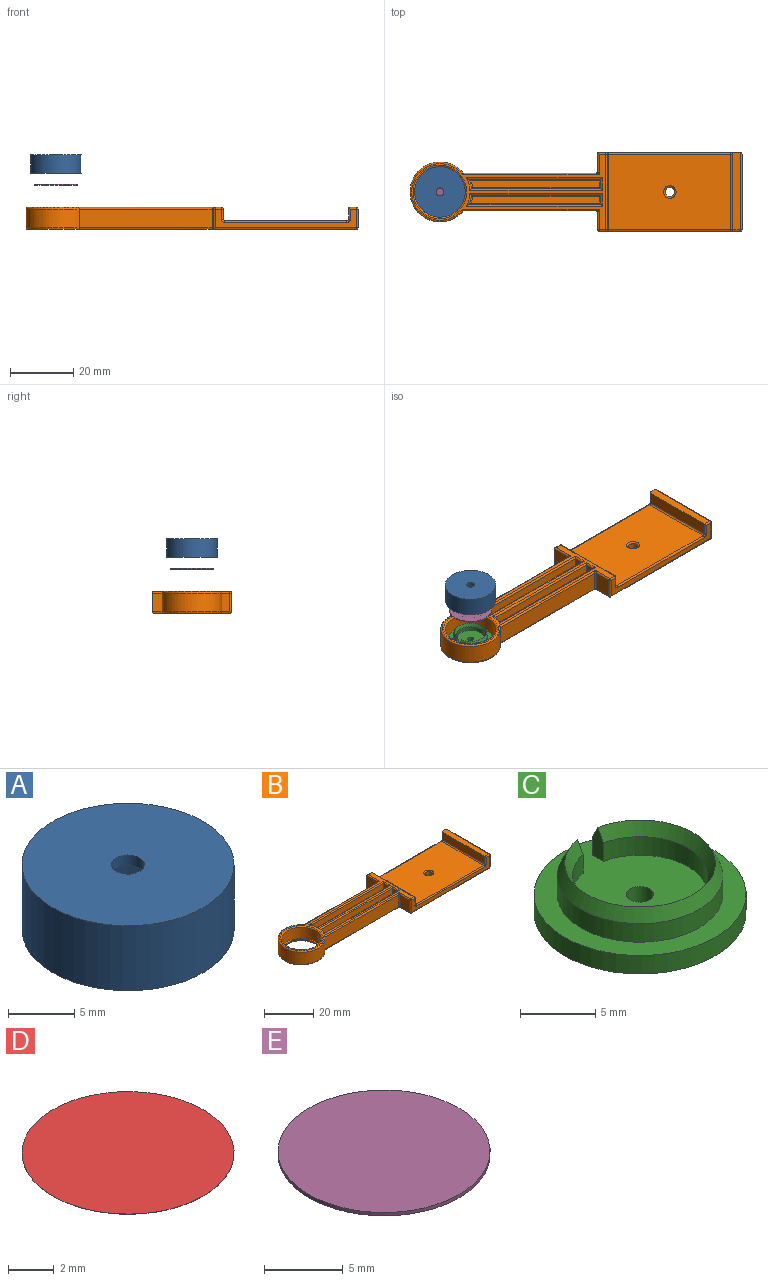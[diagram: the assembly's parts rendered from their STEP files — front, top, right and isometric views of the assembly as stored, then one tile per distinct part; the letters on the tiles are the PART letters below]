
ASSEMBLY  parts=5 mates=3
PART A: 10 faces, bbox 16x16x6 mm
  f0: plane 16x16mm, normal (0,0,-1), area 47.1mm2, adj f1,f9
  f1: cylinder r=7mm len=14mm, axis (0,0,-1), area 219.9mm2, adj f0,f2
  f2: plane 14x14mm, normal (0,0,-1), area 40.8mm2, adj f1,f3
  f3: cylinder r=6mm len=12mm, axis (0,0,-1), area 9.5mm2, adj f2,f4
  f4: cone r=5mm half-angle=54.6deg, axis (0,0,1), area 42.4mm2, adj f3,f5
  f5: cylinder r=5mm len=10mm, axis (0,0,-1), area 31.4mm2, adj f4,f6
  f6: plane 10x10mm, normal (0,0,-1), area 73.6mm2, adj f5,f7
  f7: cylinder r=1.25mm len=2.5mm, axis (0,0,-1), area 7.6mm2, adj f6,f8
  f8: plane 16x16mm, normal (0,0,1), area 196.2mm2, adj f7,f9
  f9: cylinder r=8mm len=16mm, axis (0,0,-1), area 301.6mm2, adj f0,f8
PART B: 92 faces, bbox 106.1x25x7 mm
  f0: plane 6x6mm, normal (-1,0,0), area 36mm2, adj f9,f42,f80,f81
  f1: cylinder r=8mm len=16mm, axis (0,0,1), area 276.5mm2, adj f27,f76
  f2: plane 4x3mm, normal (-1,0,0), area 12mm2, adj f20,f24,f63,f72
  f3: plane 40.6x2mm, normal (0,0,1), area 80.6mm2, adj f68,f69,f70,f71
  f4: cylinder r=10mm len=4mm, axis (0,0,1), area 12.5mm2, adj f19,f25,f64,f71
  f5: plane 61.5x24mm, normal (0,0,1), area 199.2mm2, adj f29,f30,f34,f37,f38,f42,f45,f46
  f6: plane 42.13x6mm, normal (0,-1,0), area 252.8mm2, adj f18,f30,f86,f88
  f7: plane 42.13x6mm, normal (0,1,0), area 252.8mm2, adj f18,f38,f81,f83
  f8: plane 44.8x6mm, normal (0,-1,0), area 95.8mm2, adj f28,f32,f37,f40,f44,f47,f48,f50
  f9: plane 45.3x6.5mm, normal (0,1,0), area 99.8mm2, adj f0,f15,f35,f46,f53,f55,f57,f58
  f10: cylinder r=1.5mm len=3mm, axis (0,0,-1), area 16.5mm2, adj f77,f91
  f11: plane 38.8x24mm, normal (0,0,1), area 918.6mm2, adj f51,f52,f56,f57,f77
  f12: plane 104.3x24mm, normal (0,0,-1), area 1579.5mm2, adj f31,f32,f78,f80,f82,f83,f84,f85
  f13: plane 24x3.75mm, normal (-1,0,0), area 90mm2, adj f15,f50,f56,f59
  f14: plane 24x6mm, normal (1,0,0), area 144mm2, adj f31,f35,f39,f40
  f15: plane 24.5x2.5mm, normal (0,0,1), area 61.2mm2, adj f9,f13,f39,f47,f59
  f16: plane 24x3.25mm, normal (1,0,0), area 78mm2, adj f44,f45,f52,f53
  f17: plane 6x5.5mm, normal (-1,0,0), area 33mm2, adj f28,f29,f85,f88
  f18: cylinder r=9.5mm len=19mm, axis (0,0,1), area 280.2mm2, adj f6,f7,f34,f84
  f19: plane 41.84x4mm, normal (0,1,0), area 167.3mm2, adj f4,f21,f65,f70
  f20: plane 41.84x4mm, normal (0,-1,0), area 167.3mm2, adj f2,f23,f61,f74
  f21: plane 4x3mm, normal (-1,0,0), area 12mm2, adj f19,f25,f67,f68
  f22: plane 40.6x2mm, normal (0,0,1), area 80.6mm2, adj f60,f61,f62,f63
  f23: cylinder r=10mm len=4mm, axis (0,0,1), area 12.5mm2, adj f20,f24,f60,f75
  f24: plane 41.05x4mm, normal (0,1,0), area 164.2mm2, adj f2,f23,f62,f73
  f25: plane 41.05x4mm, normal (0,-1,0), area 164.2mm2, adj f4,f21,f66,f69
  f26: cylinder r=7.5mm len=15mm, axis (0,0,-1), area 23.6mm2, adj f27,f90
  f27: plane 16x16mm, normal (0,0,1), area 24.3mm2, adj f1,f26
  f28: cylinder r=0.5mm len=6.35mm, axis (0,0,1), area 4.9mm2, adj f8,f17,f32,f33,f85
  f29: cylinder r=0.5mm len=6.5mm, axis (0,1,0), area 4.6mm2, adj f5,f17,f33,f89
  f30: cylinder r=0.5mm len=43.38mm, axis (-1,0,0), area 33.5mm2, adj f5,f6,f34,f89
  f31: cylinder r=0.5mm len=24.35mm, axis (0,1,0), area 19mm2, adj f12,f14,f35,f36,f78
  f32: cylinder r=0.5mm len=45.15mm, axis (1,0,0), area 35.3mm2, adj f8,f12,f28,f36,f85
  f33: sphere r=0.5mm, area 0.4mm2, adj f28,f29,f37
  f34: torus R=9mm, axis (0,0,1), area 36.2mm2, adj f5,f18,f30,f38
  f35: cylinder r=0.5mm len=6.85mm, axis (0,0,1), area 5.1mm2, adj f9,f14,f31,f39,f78
  f36: sphere r=0.5mm, area 0.4mm2, adj f31,f32,f40
  f37: cylinder r=0.5mm len=2mm, axis (-1,0,0), area 1.6mm2, adj f5,f8,f33,f41
  f38: cylinder r=0.5mm len=43.38mm, axis (1,0,0), area 33.5mm2, adj f5,f7,f34,f79
  f39: cylinder r=0.5mm len=24.5mm, axis (0,-1,0), area 19.1mm2, adj f14,f15,f35,f43
  f40: cylinder r=0.5mm len=6mm, axis (0,0,-1), area 4.7mm2, adj f8,f14,f36,f43
  f41: sphere r=0.5mm, area 0.4mm2, adj f37,f44,f45
  f42: cylinder r=0.5mm len=7mm, axis (0,1,0), area 4.9mm2, adj f0,f5,f46,f79
  f43: sphere r=0.5mm, area 0.4mm2, adj f39,f40,f47
  f44: cylinder r=0.5mm len=3.25mm, axis (0,0,1), area 2.6mm2, adj f8,f16,f41,f48
  f45: cylinder r=0.5mm len=24mm, axis (0,-1,0), area 18.8mm2, adj f5,f16,f41,f49
  f46: cylinder r=0.5mm len=2.5mm, axis (1,0,0), area 1.8mm2, adj f5,f9,f42,f49
  f47: cylinder r=0.5mm len=2.5mm, axis (1,0,0), area 1.8mm2, adj f8,f15,f43,f50
  f48: torus R=1mm, axis (0,-1,0), area 0.8mm2, adj f8,f44,f51,f52
  f49: sphere r=0.5mm, area 0.4mm2, adj f45,f46,f53
  f50: cylinder r=0.5mm len=3.75mm, axis (0,0,-1), area 2.8mm2, adj f8,f13,f47,f54
  f51: cylinder r=0.5mm len=38.8mm, axis (-1,0,0), area 30.5mm2, adj f8,f11,f48,f54
  f52: cylinder r=0.5mm len=24mm, axis (0,1,0), area 18.8mm2, adj f11,f16,f48,f55
  f53: cylinder r=0.5mm len=3.25mm, axis (0,0,-1), area 2.6mm2, adj f9,f16,f49,f55
  f54: torus R=1mm, axis (0,-1,0), area 0.8mm2, adj f8,f50,f51,f56
  f55: torus R=1mm, axis (0,-1,0), area 0.8mm2, adj f9,f52,f53,f57
  f56: cylinder r=0.5mm len=24mm, axis (0,-1,0), area 18.8mm2, adj f11,f13,f54,f58
  f57: cylinder r=0.5mm len=38.8mm, axis (1,0,0), area 30.5mm2, adj f9,f11,f55,f58
  f58: torus R=1mm, axis (0,-1,0), area 0.8mm2, adj f9,f56,f57,f59
  f59: cylinder r=0.5mm len=3.75mm, axis (0,0,1), area 2.9mm2, adj f9,f13,f15,f58
  f60: torus R=10.5mm, axis (0,0,-1), area 2.1mm2, adj f22,f23,f61,f62
  f61: cylinder r=0.5mm len=41.84mm, axis (-1,0,0), area 32.5mm2, adj f20,f22,f60,f63
  f62: cylinder r=0.5mm len=41.05mm, axis (-1,0,0), area 32mm2, adj f22,f24,f60,f63
  f63: cylinder r=0.5mm len=3mm, axis (0,-1,0), area 2.1mm2, adj f2,f22,f61,f62
  f64: torus R=9.5mm, axis (0,0,1), area 2.8mm2, adj f4,f5,f65,f66
  f65: cylinder r=0.5mm len=43.13mm, axis (1,0,0), area 33.2mm2, adj f5,f19,f64,f67
  f66: cylinder r=0.5mm len=42.01mm, axis (-1,0,0), area 32.5mm2, adj f5,f25,f64,f67
  f67: cylinder r=0.5mm len=4mm, axis (0,1,0), area 2.6mm2, adj f5,f21,f65,f66
  f68: cylinder r=0.5mm len=3mm, axis (0,-1,0), area 2.1mm2, adj f3,f21,f69,f70
  f69: cylinder r=0.5mm len=41.05mm, axis (1,0,0), area 32mm2, adj f3,f25,f68,f71
  f70: cylinder r=0.5mm len=41.84mm, axis (1,0,0), area 32.5mm2, adj f3,f19,f68,f71
  f71: torus R=10.5mm, axis (0,0,-1), area 2.1mm2, adj f3,f4,f69,f70
  f72: cylinder r=0.5mm len=4mm, axis (0,1,0), area 2.6mm2, adj f2,f5,f73,f74
  f73: cylinder r=0.5mm len=42.01mm, axis (1,0,0), area 32.5mm2, adj f5,f24,f72,f75
  f74: cylinder r=0.5mm len=43.13mm, axis (-1,0,0), area 33.2mm2, adj f5,f20,f72,f75
  f75: torus R=9.5mm, axis (0,0,1), area 2.8mm2, adj f5,f23,f73,f74
  f76: torus R=8.5mm, axis (0,0,1), area 40.4mm2, adj f1,f5
  f77: torus R=2mm, axis (0,0,1), area 8.3mm2, adj f10,f11
  f78: cylinder r=0.5mm len=45.65mm, axis (-1,0,0), area 35.6mm2, adj f9,f12,f31,f35,f80
  f79: bspline ~1x1mm, area 0.5mm2, adj f38,f42,f81
  f80: cylinder r=0.5mm len=6mm, axis (0,-1,0), area 4.6mm2, adj f0,f12,f78,f82
  f81: cylinder r=0.5mm len=6mm, axis (0,0,1), area 4.7mm2, adj f0,f7,f79,f82
  f82: torus R=1mm, axis (0,0,1), area 0.8mm2, adj f12,f80,f81,f83
  f83: cylinder r=0.5mm len=42.38mm, axis (-1,0,0), area 33.2mm2, adj f7,f12,f82,f84
  f84: torus R=9mm, axis (0,0,1), area 36.2mm2, adj f12,f18,f83,f86
  f85: cylinder r=0.5mm len=5.85mm, axis (0,-1,0), area 4.5mm2, adj f12,f17,f28,f32,f87
  f86: cylinder r=0.5mm len=42.38mm, axis (1,0,0), area 33.2mm2, adj f6,f12,f84,f87
  f87: torus R=1mm, axis (0,0,1), area 0.8mm2, adj f12,f85,f86,f88
  f88: cylinder r=0.5mm len=6mm, axis (0,0,-1), area 4.7mm2, adj f6,f17,f87,f89
  f89: bspline ~1x1mm, area 0.5mm2, adj f29,f30,f88
  f90: torus R=8mm, axis (0,0,1), area 37.9mm2, adj f12,f26
  f91: torus R=2mm, axis (0,0,1), area 8.3mm2, adj f10,f12
PART C: 10 faces, bbox 14.1x14.1x4 mm
  f0: cylinder r=7.04mm len=14.07mm, axis (0,0,-1), area 66.3mm2, adj f1,f6
  f1: plane 14.07x14.07mm, normal (0,0,-1), area 153mm2, adj f0,f7
  f2: cylinder r=4.5mm len=9mm, axis (0,0,-1), area 39.5mm2, adj f3,f6,f8,f9
  f3: cone r=5mm half-angle=26.6deg, axis (0,0,1), area 31.2mm2, adj f2,f4,f8,f9
  f4: cone r=5mm half-angle=26.6deg, axis (0,0,-1), area 34.7mm2, adj f3,f5,f8,f9
  f5: cylinder r=5.5mm len=11mm, axis (0,0,-1), area 49mm2, adj f4,f6,f8,f9
  f6: plane 14.07x14.07mm, normal (0,0,1), area 123.5mm2, adj f0,f2,f5,f7,f8,f9
  f7: cylinder r=0.9mm len=1.8mm, axis (0,0,1), area 8.5mm2, adj f1,f6
  f8: plane 2.51x1.02mm, normal (1,0,0), area 2mm2, adj f2,f3,f4,f5,f6
  f9: plane 2.51x1.02mm, normal (-1,0,0), area 2mm2, adj f2,f3,f4,f5,f6
PART D: 3 faces, bbox 9.3x9.3x0 mm
  f0: cylinder r=4.65mm len=9.3mm, axis (0,0,-1), area 0.3mm2, adj f1,f2
  f1: plane 9.3x9.3mm, normal (0,0,1), area 67.9mm2, adj f0
  f2: plane 9.3x9.3mm, normal (0,0,-1), area 67.9mm2, adj f0
PART E: 3 faces, bbox 13.5x13.5x0.3 mm
  f0: cylinder r=6.75mm len=13.5mm, axis (0,0,-1), area 11mm2, adj f1,f2
  f1: plane 13.5x13.5mm, normal (0,0,1), area 143.1mm2, adj f0
  f2: plane 13.5x13.5mm, normal (0,0,-1), area 143.1mm2, adj f0
PLACE A t=(5.23,10.22,16.47)mm
PLACE B t=(78.13,10.22,-8.6)mm
PLACE C rot(axis=(0,0,1),90deg) t=(5.23,10.22,-0.46)mm
PLACE D rot(axis=(1,0,0),180deg) t=(5.23,10.22,8.01)mm
PLACE E rot(axis=(1,0,0),180deg) t=(5.23,10.22,8.01)mm
MATE slider C.f0 <-> E.f0  axis (0,0,-1) through (5.23,10.22,-0.96)mm
MATE slider B.f1 <-> A.f1  axis (0,0,1) through (5.23,10.22,-5.35)mm
MATE slider E.f0 <-> A.f1  axis (0,0,1) through (5.23,10.22,8.01)mm
